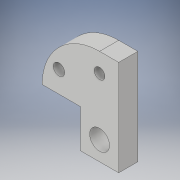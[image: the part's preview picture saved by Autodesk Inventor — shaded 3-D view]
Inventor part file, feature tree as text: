
AUTODESK INVENTOR PART (.ipt)
format: ipt  version: 2019 (Build 230136000, 136)  size: 131,584 bytes
history: native  units: in
note: dims shown in document units (in); Inventor stores cm internally (conversion verified against a paired STEP export)
features: sketch x4, hole x3, extrude x1, fillet x1
ambient origin geometry x8: Origin, YZ Plane, XZ Plane, XY Plane, X Axis, Y Axis, Z Axis, Center Point
bodies: Solid1 (feature_tree)
feature tree (9):
  extrude  "Extrusion1"  Depth=0.75in
  fillet  "Fillet1"  Radius=0.75in
  hole  "Hole1"  [1 undecoded]
  hole  "Hole2"  [1 undecoded]
  hole  "Hole3"  [1 undecoded]
  sketch  "Sketch1"  dims[d1=1.25in d2=1.0in d3=0.75in]
  sketch  "Sketch2"  dims[d4=0.5in d5=0.5in]
  sketch  "Sketch3"  dims[d8=0.25in d9=0.0in d10=0.75in]
  sketch  "Sketch4"  dims[d11=0.25in d12=0.25in d13=0.26in d14=0.276in d15=0.375in d16=0.25in d17=0.5635in d18=1.0in d19=0.8108in d20=0.25in d21=0.25in d22=0.14in d23=0.224in d24=0.375in d25=0.25in d26=0.5635in d27=0.349in d28=0.8108in d29=1.5in d30=45.0deg d31=0.15in d32=0.276in d33=0.375in d34=0.25in d35=0.5635in d36=0.432in d37=0.8108in]
note: 3 required parameter values undecoded (feature->parameter linkage not recoverable at this tier; creation-order binding heuristic only, values carry confidence <= 0.55)
